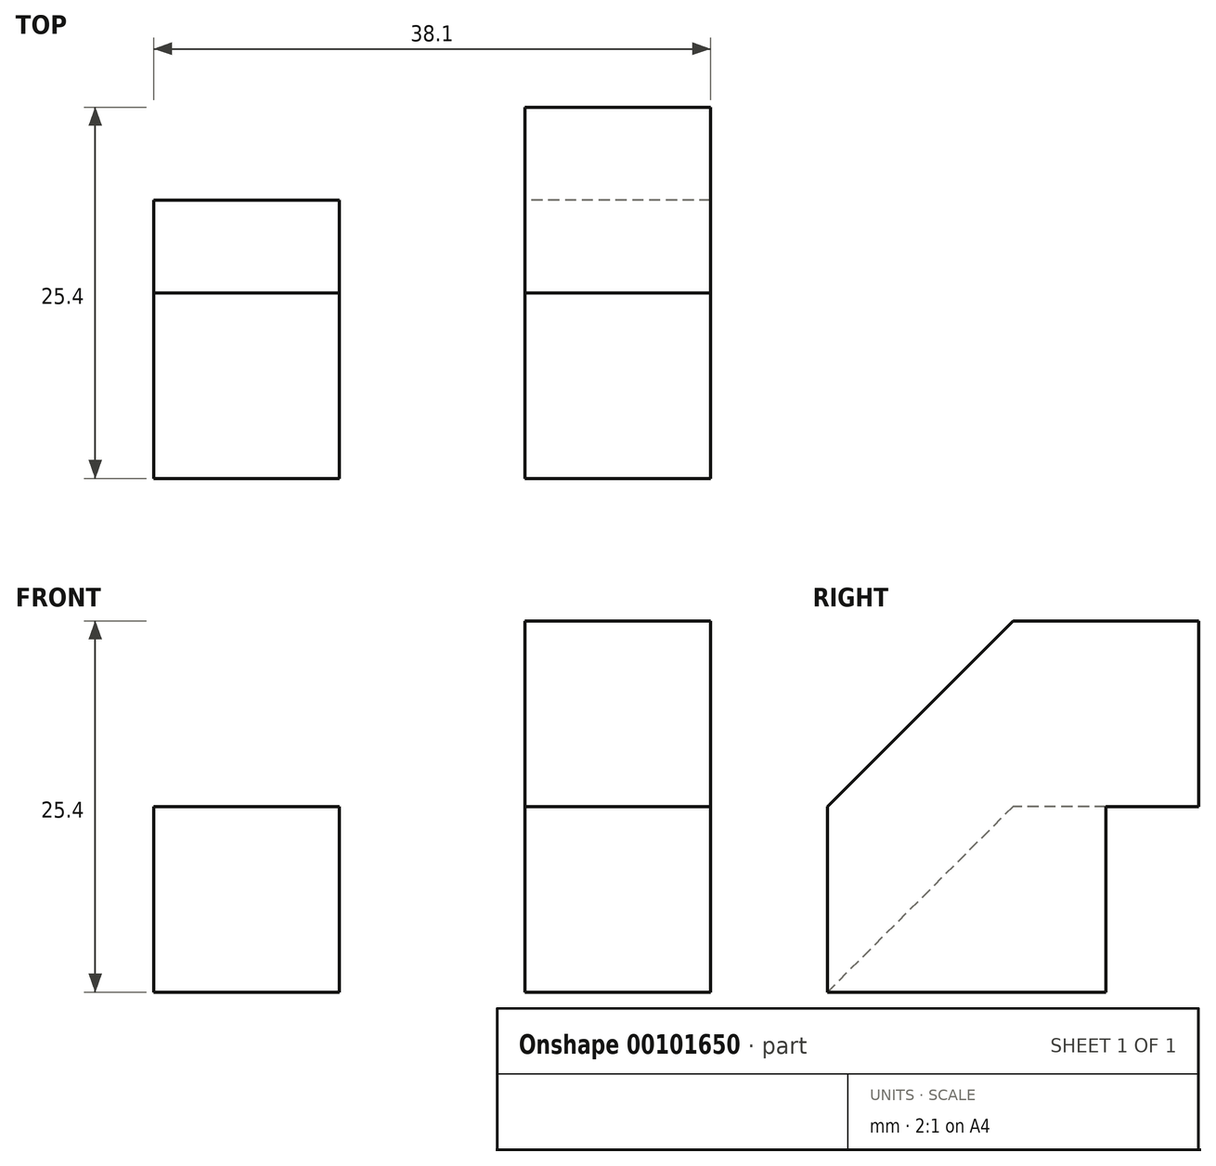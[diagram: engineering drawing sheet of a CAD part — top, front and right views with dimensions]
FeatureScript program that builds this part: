
annotation { "Feature Type Name" : "Feature", "Feature Type Description" : "" }
export const myFeature = defineFeature(function(context is Context, id is Id, definition is map)
    precondition{}
    {
        {
            var Q0;
            Q0=qCreatedBy(makeId("Right.planeOp"),FACE);
            var sketch = newSketch(context, id + "F0", { "sketchPlane" : qUnion([Q0])});
            skLineSegment(sketch, "E0", {"start": v(0, 0) * mm, "end": v(-25.4, 0) * mm});
            skLineSegment(sketch, "E1", {"start": v(-25.4, 0) * mm, "end": v(-25.4, 12.7) * mm});
            skLineSegment(sketch, "E2", {"start": v(-25.4, 12.7) * mm, "end": v(-12.7, 25.4) * mm});
            skLineSegment(sketch, "E3", {"start": v(-12.7, 25.4) * mm, "end": v(0, 25.4) * mm});
            skLineSegment(sketch, "E4", {"start": v(0, 25.4) * mm, "end": v(0, 0) * mm});
            skLineSegment(sketch, "E5", {"start": v(0, 0) * mm, "end": v(0, 12.7) * mm});
            skLineSegment(sketch, "E6", {"start": v(0, 12.7) * mm, "end": v(-12.7, 12.7) * mm});
            skLineSegment(sketch, "E7", {"start": v(-12.7, 12.7) * mm, "end": v(-25.4, 0) * mm});
            skLineSegment(sketch, "E8", {"start": v(-6.35, 12.7) * mm, "end": v(-6.35, 0) * mm});
            skSolve(sketch);
        }
        {
            var Q0;
            {var subQ0=sQuery(id+"F0.wireOp",EDGE,"E5");Q0=makeQuery(id+"F0.imprint","IMPRINT",FACE,{"disambiguationData":[TD([[makeQuery(id+"F0.imprint","IMPRINT",EDGE,{"derivedFrom":subQ0}),1.0]])]});}
            var Q1;
            {var subQ0=sQuery(id+"F0.wireOp",EDGE,"E7");Q1=makeQuery(id+"F0.imprint","IMPRINT",FACE,{"disambiguationData":[TD([[makeQuery(id+"F0.imprint","IMPRINT",EDGE,{"derivedFrom":subQ0}),1.0]])]});}
            var Q2;
            Q2=makeQuery(id+"F0.imprint","IMPRINT",FACE,{"disambiguationData":[TD([[makeQuery(id+"F0.imprint","IMPRINT",EDGE,{"derivedFrom":sQuery(id+"F0.wireOp",EDGE,"E1")}),-1.0]])]});
            extrude(context, id + "F1", {"entities" : qUnion([Q0, Q1, Q2]), "depth" : 12.7 * mm});
        }
        {
            var Q0;
            {var subQ0=sQuery(id+"F0.wireOp",EDGE,"E7");Q0=makeQuery(id+"F0.imprint","IMPRINT",FACE,{"disambiguationData":[TD([[makeQuery(id+"F0.imprint","IMPRINT",EDGE,{"derivedFrom":subQ0}),1.0]])]});}
            var Q1;
            {var subQ0=sQuery(id+"F0.wireOp",EDGE,"E5");Q1=makeQuery(id+"F0.imprint","IMPRINT",FACE,{"disambiguationData":[TD([[makeQuery(id+"F0.imprint","IMPRINT",EDGE,{"derivedFrom":subQ0}),1.0]])]});}
            extrude(context, id + "F2", {"entities" : qUnion([Q0, Q1]), "operationType" : NewBodyOperationType.ADD, "oppositeDirection" : true, "depth" : 25.4 * mm, "hasSecondDirection" : true, "secondDirectionOppositeDirection" : false, "secondDirectionDepth" : 12.7 * mm});
        }
        {
            var Q0;
            {var subQ0=sQuery(id+"F0.wireOp",EDGE,"E7");Q0=makeQuery(id+"F0.imprint","IMPRINT",FACE,{"disambiguationData":[TD([[makeQuery(id+"F0.imprint","IMPRINT",EDGE,{"derivedFrom":subQ0}),1.0]])]});}
            extrude(context, id + "F3", {"entities" : qUnion([Q0]), "operationType" : NewBodyOperationType.REMOVE, "oppositeDirection" : true, "depth" : 12.7 * mm});
        }
    });
